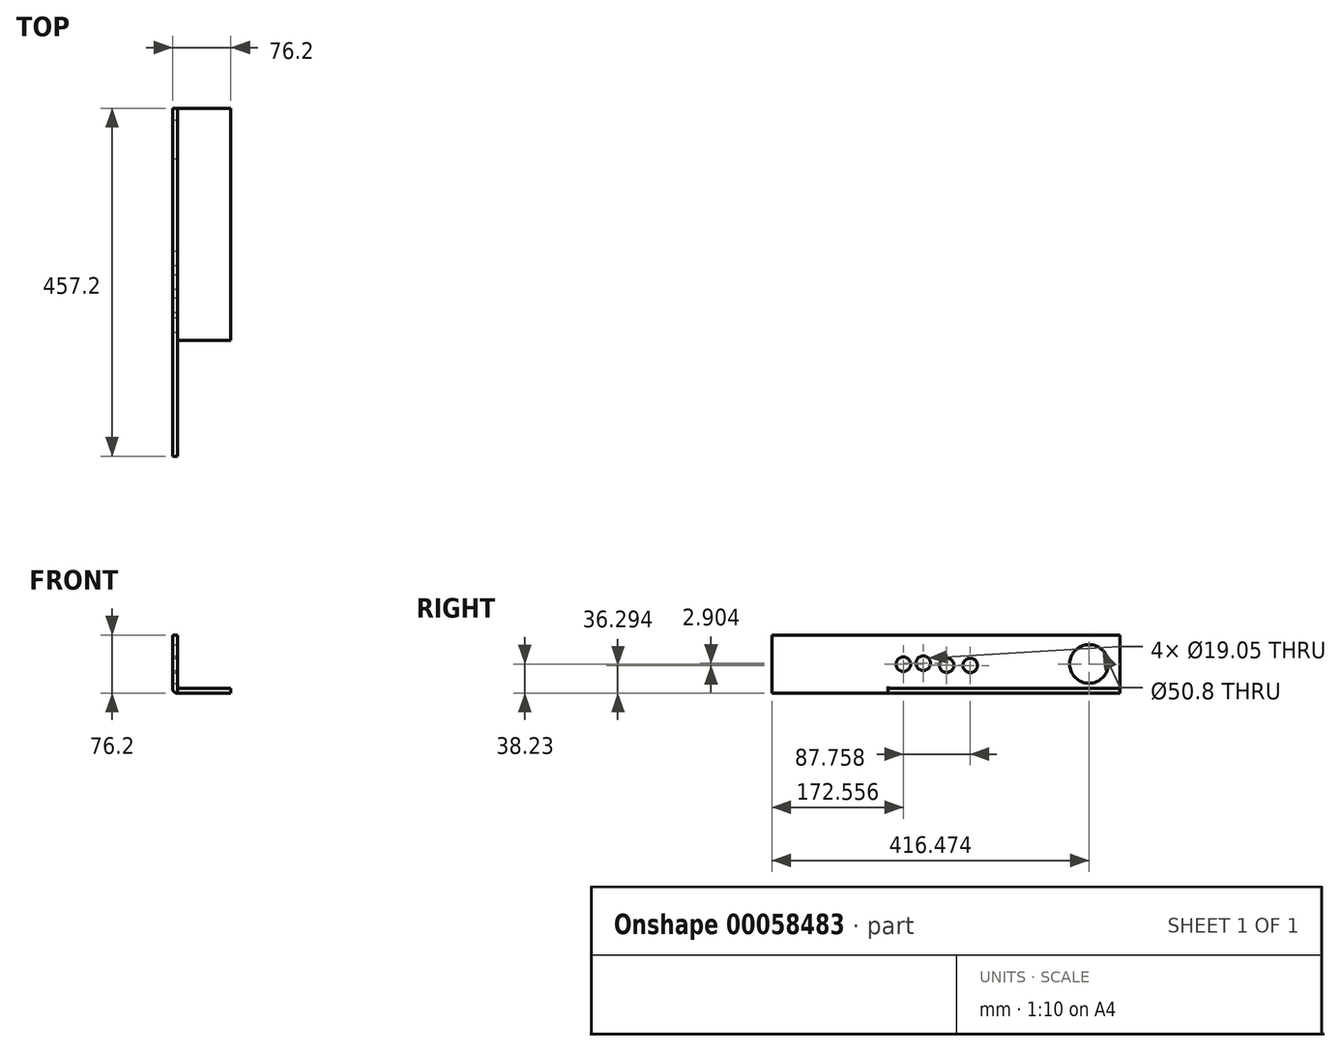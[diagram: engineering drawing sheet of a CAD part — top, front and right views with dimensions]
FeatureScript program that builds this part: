
annotation { "Feature Type Name" : "Feature", "Feature Type Description" : "" }
export const myFeature = defineFeature(function(context is Context, id is Id, definition is map)
    precondition{}
    {
        {
            var Q0;
            Q0=qCreatedBy(makeId("Top.planeOp"),FACE);
            var sketch = newSketch(context, id + "F0", { "sketchPlane" : qUnion([Q0])});
            skLineSegment(sketch, "E0.bottom", {"start": v(0, 0) * mm, "end": v(76.2, 0) * mm});
            skLineSegment(sketch, "E0.top", {"start": v(0, -304.8) * mm, "end": v(76.2, -304.8) * mm});
            skLineSegment(sketch, "E0.left", {"start": v(0, 0) * mm, "end": v(0, -304.8) * mm});
            skLineSegment(sketch, "E0.right", {"start": v(76.2, 0) * mm, "end": v(76.2, -304.8) * mm});
            skSolve(sketch);
        }
        {
            var Q0;
            Q0=makeQuery(id+"F0.imprint","IMPRINT",FACE,{"disambiguationData":[TD([[makeQuery(id+"F0.imprint","IMPRINT",EDGE,{"derivedFrom":sQuery(id+"F0.wireOp",EDGE,"E0.bottom")}),-1.0]])]});
            extrude(context, id + "F1", {"entities" : qUnion([Q0]), "depth" : 6.35 * mm});
        }
        {
            var Q0;
            Q0=qCreatedBy(makeId("Right.planeOp"),FACE);
            var sketch = newSketch(context, id + "F2", { "sketchPlane" : qUnion([Q0])});
            skLineSegment(sketch, "E1.bottom", {"start": v(0, 0) * mm, "end": v(-457.2, 0) * mm});
            skLineSegment(sketch, "E1.top", {"start": v(0, 76.2) * mm, "end": v(-457.2, 76.2) * mm});
            skLineSegment(sketch, "E1.left", {"start": v(0, 0) * mm, "end": v(0, 76.2) * mm});
            skLineSegment(sketch, "E1.right", {"start": v(-457.2, 0) * mm, "end": v(-457.2, 76.2) * mm});
            skSolve(sketch);
        }
        {
            var Q0;
            Q0=makeQuery(id+"F2.imprint","IMPRINT",FACE,{"disambiguationData":[TD([[makeQuery(id+"F2.imprint","IMPRINT",EDGE,{"derivedFrom":sQuery(id+"F2.wireOp",EDGE,"E1.bottom")}),-1.0]])]});
            extrude(context, id + "F3", {"entities" : qUnion([Q0]), "operationType" : NewBodyOperationType.ADD, "depth" : 6.35 * mm});
        }
        {
            var Q0;
            Q0=makeQuery(id+"F1.opExtrude","CAP_EDGE",EDGE,{"disambiguationData":[OSD([sQuery(id+"F0.wireOp",EDGE,"E0.left")])],"isStart":true});
            fillet(context, id + "F4", {"entities" : qUnion([Q0]), "radius" : 5.08 * mm, "tangentPropagation" : true, "allowEdgeOverflow" : false});
        }
        {
            var Q0;
            Q0=makeQuery(id+"F3.boolean.opBoolean","INTERSECT",EDGE,{"derivedFrom":[makeQuery(id+"F1.opExtrude","CAP_FACE",FACE,{"disambiguationData":[OSD([sQuery(id+"F0.wireOp",EDGE,"E0.bottom"),sQuery(id+"F0.wireOp",EDGE,"E0.top"),sQuery(id+"F0.wireOp",EDGE,"E0.left"),sQuery(id+"F0.wireOp",EDGE,"E0.right")])],"isStart":false}),makeQuery(id+"F3.opExtrude","CAP_FACE",FACE,{"disambiguationData":[OSD([sQuery(id+"F2.wireOp",EDGE,"E1.bottom"),sQuery(id+"F2.wireOp",EDGE,"E1.top"),sQuery(id+"F2.wireOp",EDGE,"E1.left"),sQuery(id+"F2.wireOp",EDGE,"E1.right")])],"isStart":false})]});
            fillet(context, id + "F5", {"entities" : qUnion([Q0]), "radius" : 2.54 * mm, "rho" : 0.5, "crossSection" : FilletCrossSection.CONIC, "allowEdgeOverflow" : false});
        }
        {
            var Q0;
            Q0=makeQuery(id+"F3.opExtrude","CAP_FACE",FACE,{"disambiguationData":[OSD([sQuery(id+"F2.wireOp",EDGE,"E1.bottom"),sQuery(id+"F2.wireOp",EDGE,"E1.top"),sQuery(id+"F2.wireOp",EDGE,"E1.left"),sQuery(id+"F2.wireOp",EDGE,"E1.right")])],"isStart":false});
            var sketch = newSketch(context, id + "F6", { "sketchPlane" : qUnion([Q0])});
            skCircle(sketch, "E2", {"center": v(-284.64, 37.9) * mm, "radius": 9.53 * mm});
            skCircle(sketch, "E3", {"center": v(-50.8, 38.23) * mm, "radius": 25.4 * mm});
            skSolve(sketch);
        }
        {
            var Q0;
            Q0=makeQuery(id+"F6.imprint","IMPRINT",FACE,{"disambiguationData":[TD([[makeQuery(id+"F6.imprint","IMPRINT",EDGE,{"derivedFrom":sQuery(id+"F6.wireOp",EDGE,"E2")}),1.0]])]});
            extrude(context, id + "F7", {"entities" : qUnion([Q0]), "operationType" : NewBodyOperationType.REMOVE, "oppositeDirection" : true, "depth" : 25.4 * mm});
        }
        {
            var Q0;
            Q0=makeQuery(id+"F3.opExtrude","CAP_FACE",FACE,{"disambiguationData":[OSD([sQuery(id+"F2.wireOp",EDGE,"E1.bottom"),sQuery(id+"F2.wireOp",EDGE,"E1.top"),sQuery(id+"F2.wireOp",EDGE,"E1.left"),sQuery(id+"F2.wireOp",EDGE,"E1.right")])],"isStart":false});
            var sketch = newSketch(context, id + "F8", { "sketchPlane" : qUnion([Q0])});
            skCircle(sketch, "E4", {"center": v(-258.51, 39.2) * mm, "radius": 9.53 * mm});
            skSolve(sketch);
        }
        {
            var Q0;
            Q0 = qSketchRegion(id + "F8", true);
            extrude(context, id + "F9", {"entities" : qUnion([Q0]), "operationType" : NewBodyOperationType.REMOVE, "oppositeDirection" : true, "depth" : 25.4 * mm});
        }
        {
            var Q0;
            Q0=makeQuery(id+"F3.opExtrude","CAP_FACE",FACE,{"disambiguationData":[OSD([sQuery(id+"F2.wireOp",EDGE,"E1.bottom"),sQuery(id+"F2.wireOp",EDGE,"E1.top"),sQuery(id+"F2.wireOp",EDGE,"E1.left"),sQuery(id+"F2.wireOp",EDGE,"E1.right")])],"isStart":false});
            var sketch = newSketch(context, id + "F10", { "sketchPlane" : qUnion([Q0])});
            skCircle(sketch, "E5", {"center": v(-227.86, 36.62) * mm, "radius": 9.53 * mm});
            skSolve(sketch);
        }
        {
            var Q0;
            Q0 = qSketchRegion(id + "F10", true);
            extrude(context, id + "F11", {"entities" : qUnion([Q0]), "operationType" : NewBodyOperationType.REMOVE, "oppositeDirection" : true, "depth" : 25.4 * mm});
        }
        {
            var Q0;
            Q0=makeQuery(id+"F3.opExtrude","CAP_FACE",FACE,{"disambiguationData":[OSD([sQuery(id+"F2.wireOp",EDGE,"E1.bottom"),sQuery(id+"F2.wireOp",EDGE,"E1.top"),sQuery(id+"F2.wireOp",EDGE,"E1.left"),sQuery(id+"F2.wireOp",EDGE,"E1.right")])],"isStart":false});
            var sketch = newSketch(context, id + "F12", { "sketchPlane" : qUnion([Q0])});
            skCircle(sketch, "E6", {"center": v(-196.89, 36.3) * mm, "radius": 9.53 * mm});
            skSolve(sketch);
        }
        {
            var Q0;
            Q0=makeQuery(id+"F12.imprint","IMPRINT",FACE,{"disambiguationData":[TD([[makeQuery(id+"F12.imprint","IMPRINT",EDGE,{"derivedFrom":sQuery(id+"F12.wireOp",EDGE,"E6")}),1.0]])]});
            extrude(context, id + "F13", {"entities" : qUnion([Q0]), "operationType" : NewBodyOperationType.REMOVE, "oppositeDirection" : true, "depth" : 25.4 * mm});
        }
        {
            var Q0;
            Q0=makeQuery(id+"F3.opExtrude","CAP_FACE",FACE,{"disambiguationData":[OSD([sQuery(id+"F2.wireOp",EDGE,"E1.bottom"),sQuery(id+"F2.wireOp",EDGE,"E1.top"),sQuery(id+"F2.wireOp",EDGE,"E1.left"),sQuery(id+"F2.wireOp",EDGE,"E1.right")])],"isStart":false});
            var sketch = newSketch(context, id + "F14", { "sketchPlane" : qUnion([Q0])});
            skCircle(sketch, "E7", {"center": v(-40.73, 38.23) * mm, "radius": 25.4 * mm});
            skSolve(sketch);
        }
        {
            var Q0;
            Q0=makeQuery(id+"F14.imprint","IMPRINT",FACE,{"disambiguationData":[TD([[makeQuery(id+"F14.imprint","IMPRINT",EDGE,{"derivedFrom":sQuery(id+"F14.wireOp",EDGE,"E7")}),1.0]])]});
            extrude(context, id + "F15", {"entities" : qUnion([Q0]), "operationType" : NewBodyOperationType.REMOVE, "oppositeDirection" : true, "depth" : 25.4 * mm});
        }
    });
